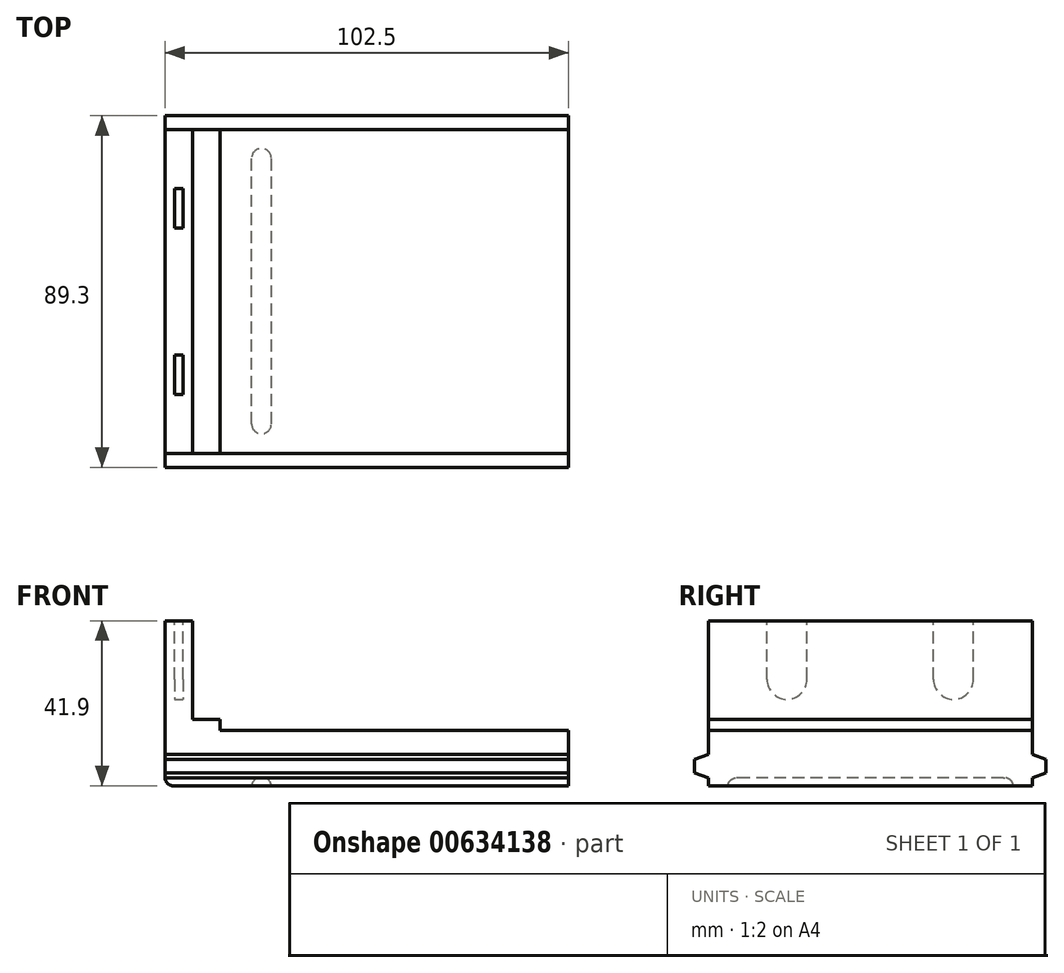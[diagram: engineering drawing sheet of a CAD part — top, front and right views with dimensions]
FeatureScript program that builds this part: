
annotation { "Feature Type Name" : "Feature", "Feature Type Description" : "" }
export const myFeature = defineFeature(function(context is Context, id is Id, definition is map)
    precondition{}
    {
        {
            var Q0;
            Q0=qCreatedBy(makeId("Top.planeOp"),FACE);
            var sketch = newSketch(context, id + "F0", { "sketchPlane" : qUnion([Q0])});
            skLineSegment(sketch, "E0.bottom", {"start": v(-51.25, 41.15) * mm, "end": v(51.25, 41.15) * mm});
            skLineSegment(sketch, "E0.top", {"start": v(-51.25, -41.15) * mm, "end": v(51.25, -41.15) * mm});
            skLineSegment(sketch, "E0.left", {"start": v(-51.25, 41.15) * mm, "end": v(-51.25, -41.15) * mm});
            skLineSegment(sketch, "E0.right", {"start": v(51.25, 41.15) * mm, "end": v(51.25, -41.15) * mm});
            skSolve(sketch);
        }
        {
            var Q0;
            Q0=makeQuery(id+"F0.imprint","IMPRINT",FACE,{"disambiguationData":[TD([[makeQuery(id+"F0.imprint","IMPRINT",EDGE,{"derivedFrom":sQuery(id+"F0.wireOp",EDGE,"E0.bottom")}),-1.0]])]});
            extrude(context, id + "F1", {"entities" : qUnion([Q0]), "depth" : 14 * mm, "offsetDistance" : 25 * mm});
        }
        {
            var Q0;
            Q0=makeQuery(id+"F1.opExtrude","CAP_FACE",FACE,{"disambiguationData":[OSD([sQuery(id+"F0.wireOp",EDGE,"E0.bottom"),sQuery(id+"F0.wireOp",EDGE,"E0.top"),sQuery(id+"F0.wireOp",EDGE,"E0.left"),sQuery(id+"F0.wireOp",EDGE,"E0.right")])],"isStart":false});
            var sketch = newSketch(context, id + "F2", { "sketchPlane" : qUnion([Q0])});
            skLineSegment(sketch, "E1.bottom", {"start": v(-51.25, 41.15) * mm, "end": v(-44.25, 41.15) * mm});
            skLineSegment(sketch, "E1.top", {"start": v(-51.25, -41.15) * mm, "end": v(-44.25, -41.15) * mm});
            skLineSegment(sketch, "E1.left", {"start": v(-51.25, 41.15) * mm, "end": v(-51.25, -41.15) * mm});
            skLineSegment(sketch, "E1.right", {"start": v(-44.25, 41.15) * mm, "end": v(-44.25, -41.15) * mm});
            skSolve(sketch);
        }
        {
            var Q0;
            Q0=makeQuery(id+"F2.imprint","IMPRINT",FACE,{"disambiguationData":[TD([[makeQuery(id+"F2.imprint","IMPRINT",EDGE,{"derivedFrom":sQuery(id+"F2.wireOp",EDGE,"E1.bottom")}),-1.0]])]});
            extrude(context, id + "F3", {"entities" : qUnion([Q0]), "operationType" : NewBodyOperationType.ADD, "depth" : 27.9 * mm, "offsetDistance" : 25 * mm});
        }
        {
            var Q0;
            Q0=makeQuery(id+"F1.opExtrude","CAP_FACE",FACE,{"disambiguationData":[OSD([sQuery(id+"F0.wireOp",EDGE,"E0.bottom"),sQuery(id+"F0.wireOp",EDGE,"E0.top"),sQuery(id+"F0.wireOp",EDGE,"E0.left"),sQuery(id+"F0.wireOp",EDGE,"E0.right")])],"isStart":false});
            var sketch = newSketch(context, id + "F4", { "sketchPlane" : qUnion([Q0])});
            skLineSegment(sketch, "E2.bottom", {"start": v(-44.25, 41.15) * mm, "end": v(-37.25, 41.15) * mm});
            skLineSegment(sketch, "E2.top", {"start": v(-44.25, -41.15) * mm, "end": v(-37.25, -41.15) * mm});
            skLineSegment(sketch, "E2.left", {"start": v(-44.25, 41.15) * mm, "end": v(-44.25, -41.15) * mm});
            skLineSegment(sketch, "E2.right", {"start": v(-37.25, 41.15) * mm, "end": v(-37.25, -41.15) * mm});
            skSolve(sketch);
        }
        {
            var Q0;
            Q0=makeQuery(id+"F4.imprint","IMPRINT",FACE,{"disambiguationData":[TD([[makeQuery(id+"F4.imprint","IMPRINT",EDGE,{"derivedFrom":sQuery(id+"F4.wireOp",EDGE,"E2.bottom")}),-1.0]])]});
            extrude(context, id + "F5", {"entities" : qUnion([Q0]), "operationType" : NewBodyOperationType.ADD, "depth" : 2.9 * mm, "offsetDistance" : 25 * mm});
        }
        {
            var Q0;
            Q0=makeQuery(id+"F1.opExtrude","SWEPT_FACE",FACE,{"disambiguationData":[OSD([sQuery(id+"F0.wireOp",EDGE,"E0.right")])]});
            var sketch = newSketch(context, id + "F6", { "sketchPlane" : qUnion([Q0])});
            skLineSegment(sketch, "E3", {"start": v(41.15, 2) * mm, "end": v(44.65, 3.27) * mm});
            skLineSegment(sketch, "E4", {"start": v(44.65, 3.27) * mm, "end": v(44.65, 6.73) * mm});
            skLineSegment(sketch, "E5", {"start": v(44.65, 6.73) * mm, "end": v(41.15, 8) * mm});
            skLineSegment(sketch, "E6", {"start": v(-41.15, 2) * mm, "end": v(-44.65, 3.27) * mm});
            skLineSegment(sketch, "E7", {"start": v(-44.65, 3.27) * mm, "end": v(-44.65, 6.73) * mm});
            skLineSegment(sketch, "E8", {"start": v(-44.65, 6.73) * mm, "end": v(-41.15, 8) * mm});
            skSolve(sketch);
        }
        {
            var Q0;
            {var subQ0=sQuery(id+"F6.wireOp",EDGE,"E3");Q0=makeQuery(id+"F6.imprint","IMPRINT",FACE,{"disambiguationData":[TD([[makeQuery(id+"F6.imprint","IMPRINT",EDGE,{"derivedFrom":subQ0}),1.0]])]});}
            var Q1;
            {var subQ0=sQuery(id+"F6.wireOp",EDGE,"E6");Q1=makeQuery(id+"F6.imprint","IMPRINT",FACE,{"disambiguationData":[TD([[makeQuery(id+"F6.imprint","IMPRINT",EDGE,{"derivedFrom":subQ0}),-1.0]])]});}
            extrude(context, id + "F7", {"entities" : qUnion([Q0, Q1]), "depth" : -102.5 * mm, "offsetDistance" : 25 * mm});
        }
        {
            var Q0;
            Q0=makeQuery(id+"F1.opExtrude","CAP_EDGE",EDGE,{"disambiguationData":[OSD([sQuery(id+"F0.wireOp",EDGE,"E0.left")])],"isStart":true});
            fillet(context, id + "F8", {"entities" : qUnion([Q0]), "radius" : 2 * mm, "tangentPropagation" : true, "allowEdgeOverflow" : false});
        }
        {
            var Q0;
            Q0=makeQuery(id+"F1.opExtrude","CAP_FACE",FACE,{"disambiguationData":[OSD([sQuery(id+"F0.wireOp",EDGE,"E0.bottom"),sQuery(id+"F0.wireOp",EDGE,"E0.top"),sQuery(id+"F0.wireOp",EDGE,"E0.left"),sQuery(id+"F0.wireOp",EDGE,"E0.right")])],"isStart":true});
            var sketch = newSketch(context, id + "F9", { "sketchPlane" : qUnion([Q0])});
            skLineSegment(sketch, "E9", {"start": v(-29.25, 33.65) * mm, "end": v(-29.25, -33.85) * mm});
            skLineSegment(sketch, "E10", {"start": v(-24.25, 33.65) * mm, "end": v(-24.25, -33.85) * mm});
            skArc(sketch, "E11", {"start": v(-29.25, 33.65) * mm, "mid": v(-26.75, 36.15) * mm, "end": v(-24.25, 33.65) * mm});
            skArc(sketch, "E12", {"start": v(-29.25, -33.85) * mm, "mid": v(-26.75, -36.35) * mm, "end": v(-24.25, -33.85) * mm});
            skSolve(sketch);
        }
        {
            var Q0;
            Q0=makeQuery(id+"F7.opExtrude","SWEPT_BODY",BODY,{"disambiguationData":[OSD([sQuery(id+"F0.wireOp",EDGE,"E0.bottom"),sQuery(id+"F0.wireOp",EDGE,"E0.right"),sQuery(id+"F6.wireOp",EDGE,"E3"),sQuery(id+"F6.wireOp",EDGE,"E4"),sQuery(id+"F6.wireOp",EDGE,"E5")])]});
            var Q1;
            Q1=makeQuery(id+"F1.opExtrude","SWEPT_BODY",BODY,{"disambiguationData":[OSD([sQuery(id+"F0.wireOp",EDGE,"E0.bottom"),sQuery(id+"F0.wireOp",EDGE,"E0.top"),sQuery(id+"F0.wireOp",EDGE,"E0.left"),sQuery(id+"F0.wireOp",EDGE,"E0.right")])]});
            var Q2;
            Q2=makeQuery(id+"F7.opExtrude","SWEPT_BODY",BODY,{"disambiguationData":[OSD([sQuery(id+"F0.wireOp",EDGE,"E0.top"),sQuery(id+"F0.wireOp",EDGE,"E0.right"),sQuery(id+"F6.wireOp",EDGE,"E6"),sQuery(id+"F6.wireOp",EDGE,"E7"),sQuery(id+"F6.wireOp",EDGE,"E8")])]});
            booleanBodies(context, id + "F10", {"operationType" : BooleanOperationType.UNION, "tools" : qUnion([Q0, Q1, Q2])});
        }
        {
            var Q0;
            Q0=makeQuery(id+"F9.imprint","IMPRINT",FACE,{"disambiguationData":[TD([[makeQuery(id+"F9.imprint","IMPRINT",EDGE,{"derivedFrom":sQuery(id+"F9.wireOp",EDGE,"E9")}),1.0]])]});
            extrude(context, id + "F11", {"entities" : qUnion([Q0]), "operationType" : NewBodyOperationType.REMOVE, "oppositeDirection" : true, "depth" : 2 * mm, "offsetDistance" : 25 * mm});
        }
        {
            var Q0;
            Q0=makeQuery(id+"F11.boolean.opBoolean","COPY",EDGE,{"derivedFrom":makeQuery(id+"F11.opExtrude","CAP_EDGE",EDGE,{"disambiguationData":[OSD([sQuery(id+"F9.wireOp",EDGE,"E9")])],"isStart":false})});
            var Q1;
            Q1=makeQuery(id+"F11.boolean.opBoolean","COPY",EDGE,{"derivedFrom":makeQuery(id+"F11.opExtrude","CAP_EDGE",EDGE,{"disambiguationData":[OSD([sQuery(id+"F9.wireOp",EDGE,"E10")])],"isStart":false})});
            fillet(context, id + "F12", {"entities" : qUnion([Q0, Q1]), "radius" : 2.2 * mm, "tangentPropagation" : true, "allowEdgeOverflow" : false});
        }
        {
            var Q0;
            Q0=makeQuery(id+"F3.opExtrude","CAP_FACE",FACE,{"disambiguationData":[OSD([sQuery(id+"F2.wireOp",EDGE,"E1.bottom"),sQuery(id+"F2.wireOp",EDGE,"E1.top"),sQuery(id+"F2.wireOp",EDGE,"E1.left"),sQuery(id+"F2.wireOp",EDGE,"E1.right")])],"isStart":false});
            var sketch = newSketch(context, id + "F13", { "sketchPlane" : qUnion([Q0])});
            skLineSegment(sketch, "E13.bottom", {"start": v(-48.8, 26.2) * mm, "end": v(-46.7, 26.2) * mm});
            skLineSegment(sketch, "E13.top", {"start": v(-48.8, 16.1) * mm, "end": v(-46.7, 16.1) * mm});
            skLineSegment(sketch, "E13.left", {"start": v(-48.8, 26.2) * mm, "end": v(-48.8, 16.1) * mm});
            skLineSegment(sketch, "E13.right", {"start": v(-46.7, 26.2) * mm, "end": v(-46.7, 16.1) * mm});
            skLineSegment(sketch, "E14.bottom", {"start": v(-48.8, -16.1) * mm, "end": v(-46.7, -16.1) * mm});
            skLineSegment(sketch, "E14.top", {"start": v(-48.8, -26.2) * mm, "end": v(-46.7, -26.2) * mm});
            skLineSegment(sketch, "E14.left", {"start": v(-48.8, -16.1) * mm, "end": v(-48.8, -26.2) * mm});
            skLineSegment(sketch, "E14.right", {"start": v(-46.7, -16.1) * mm, "end": v(-46.7, -26.2) * mm});
            skSolve(sketch);
        }
        {
            var Q0;
            Q0=makeQuery(id+"F13.imprint","IMPRINT",FACE,{"disambiguationData":[TD([[makeQuery(id+"F13.imprint","IMPRINT",EDGE,{"derivedFrom":sQuery(id+"F13.wireOp",EDGE,"E13.bottom")}),-1.0]])]});
            var Q1;
            Q1=makeQuery(id+"F13.imprint","IMPRINT",FACE,{"disambiguationData":[TD([[makeQuery(id+"F13.imprint","IMPRINT",EDGE,{"derivedFrom":sQuery(id+"F13.wireOp",EDGE,"E14.bottom")}),-1.0]])]});
            extrude(context, id + "F14", {"entities" : qUnion([Q0, Q1]), "operationType" : NewBodyOperationType.REMOVE, "oppositeDirection" : true, "depth" : 19.95 * mm, "offsetDistance" : 25 * mm});
        }
        {
            var Q0;
            Q0=makeQuery(id+"F14.boolean.opBoolean","COPY",EDGE,{"derivedFrom":makeQuery(id+"F14.opExtrude","CAP_EDGE",EDGE,{"disambiguationData":[OSD([sQuery(id+"F13.wireOp",EDGE,"E13.top")])],"isStart":false})});
            var Q1;
            Q1=makeQuery(id+"F14.boolean.opBoolean","COPY",EDGE,{"derivedFrom":makeQuery(id+"F14.opExtrude","CAP_EDGE",EDGE,{"disambiguationData":[OSD([sQuery(id+"F13.wireOp",EDGE,"E13.bottom")])],"isStart":false})});
            fillet(context, id + "F15", {"entities" : qUnion([Q0, Q1]), "radius" : 5.05 * mm, "tangentPropagation" : true, "allowEdgeOverflow" : false});
        }
        {
            var Q0;
            Q0=makeQuery(id+"F14.boolean.opBoolean","COPY",EDGE,{"derivedFrom":makeQuery(id+"F14.opExtrude","CAP_EDGE",EDGE,{"disambiguationData":[OSD([sQuery(id+"F13.wireOp",EDGE,"E14.bottom")])],"isStart":false})});
            var Q1;
            Q1=makeQuery(id+"F14.boolean.opBoolean","COPY",EDGE,{"derivedFrom":makeQuery(id+"F14.opExtrude","CAP_EDGE",EDGE,{"disambiguationData":[OSD([sQuery(id+"F13.wireOp",EDGE,"E14.top")])],"isStart":false})});
            fillet(context, id + "F16", {"entities" : qUnion([Q0, Q1]), "radius" : 5.05 * mm, "tangentPropagation" : true, "allowEdgeOverflow" : false});
        }
    });
